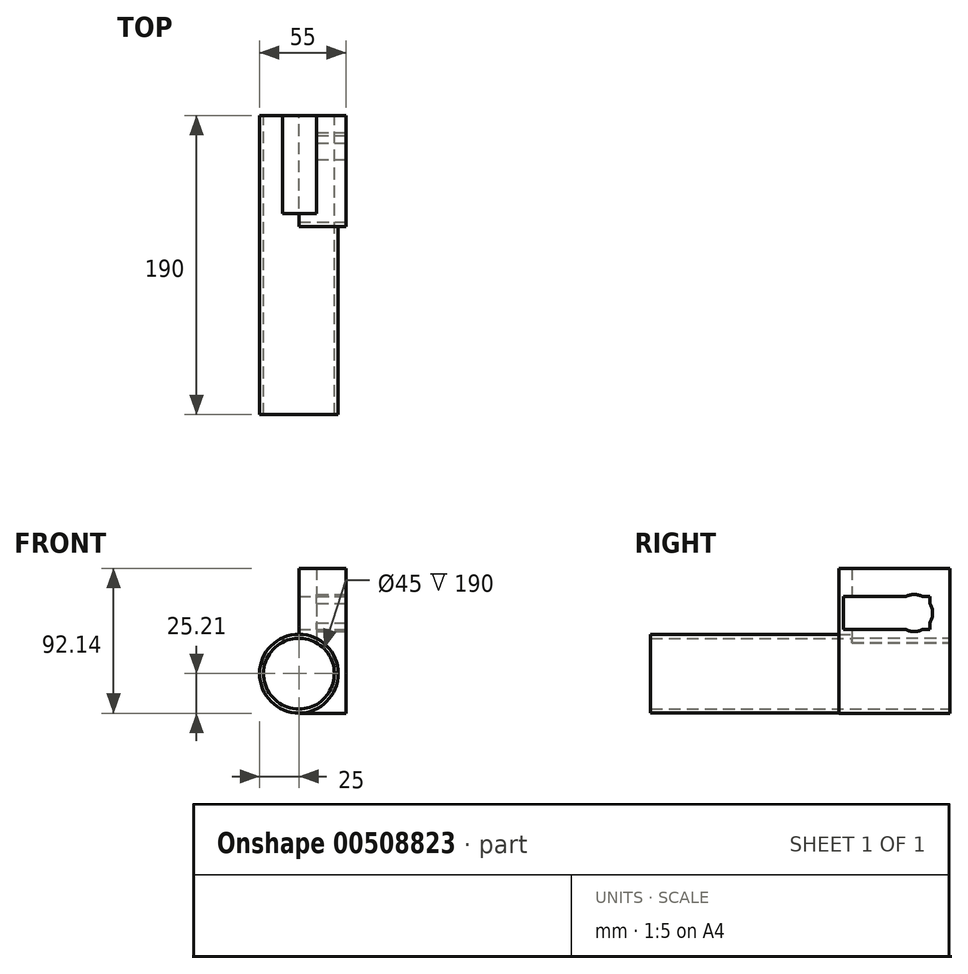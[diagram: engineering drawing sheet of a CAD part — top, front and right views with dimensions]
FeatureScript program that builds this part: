
annotation { "Feature Type Name" : "Feature", "Feature Type Description" : "" }
export const myFeature = defineFeature(function(context is Context, id is Id, definition is map)
    precondition{}
    {
        {
            var Q0;
            Q0=qCreatedBy(makeId("Front.planeOp"),FACE);
            var sketch = newSketch(context, id + "F0", { "sketchPlane" : qUnion([Q0])});
            skCircle(sketch, "E0", {"center": v(0, 0) * mm, "radius": 22.5 * mm});
            skCircle(sketch, "E1", {"center": v(0, 0) * mm, "radius": 25 * mm});
            skSolve(sketch);
        }
        {
            var Q0;
            Q0 = qSketchRegion(id + "F0", true);
            extrude(context, id + "F1", {"entities" : qUnion([Q0]), "depth" : 190 * mm});
        }
        {
            var Q0;
            Q0=qCreatedBy(makeId("Right.planeOp"),FACE);
            var sketch = newSketch(context, id + "F2", { "sketchPlane" : qUnion([Q0])});
            skLineSegment(sketch, "E2.bottom", {"start": v(-70.47, 66.93) * mm, "end": v(0, 66.93) * mm});
            skLineSegment(sketch, "E2.top", {"start": v(-70.47, -25.2) * mm, "end": v(0, -25.2) * mm});
            skLineSegment(sketch, "E2.left", {"start": v(-70.47, 66.93) * mm, "end": v(-70.47, -25.2) * mm});
            skLineSegment(sketch, "E2.right", {"start": v(0, 66.93) * mm, "end": v(0, -25.2) * mm});
            skSolve(sketch);
        }
        {
            var Q0;
            Q0 = qSketchRegion(id + "F2", true);
            extrude(context, id + "F3", {"entities" : qUnion([Q0]), "operationType" : NewBodyOperationType.ADD, "depth" : 30 * mm, "offsetDistance" : 25 * mm});
        }
        {
            var Q0;
            Q0=makeQuery(id+"F3.boolean.opBoolean","SPLIT",FACE,{"disambiguationData":[TD([makeQuery(id+"F1.opExtrude","SWEPT_FACE",FACE,{"disambiguationData":[OSD([sQuery(id+"F0.wireOp",EDGE,"E0")])]})])],"derivedFrom":makeQuery(id+"F3.opExtrude","SWEPT_FACE",FACE,{"disambiguationData":[OSD([sQuery(id+"F2.wireOp",EDGE,"E2.left")])]})});
            var sketch = newSketch(context, id + "F4", { "sketchPlane" : qUnion([Q0])});
            skCircle(sketch, "E3", {"center": v(0, 0) * mm, "radius": 22.5 * mm});
            skSolve(sketch);
        }
        {
            var Q0;
            Q0 = qSketchRegion(id + "F4", true);
            extrude(context, id + "F5", {"entities" : qUnion([Q0]), "operationType" : NewBodyOperationType.REMOVE, "endBound" : BoundingType.SYMMETRIC, "depth" : 200 * mm});
        }
        {
            var Q0;
            Q0=qCreatedBy(makeId("Top.planeOp"),FACE);
            var sketch = newSketch(context, id + "F6", { "sketchPlane" : qUnion([Q0])});
            skLineSegment(sketch, "E4.bottom", {"start": v(11.28, -62.15) * mm, "end": v(-10.5, -62.15) * mm});
            skLineSegment(sketch, "E4.top", {"start": v(11.28, 0) * mm, "end": v(-10.5, 0) * mm});
            skLineSegment(sketch, "E4.left", {"start": v(11.28, -62.15) * mm, "end": v(11.28, 0) * mm});
            skLineSegment(sketch, "E4.right", {"start": v(-10.5, -62.15) * mm, "end": v(-10.5, 0) * mm});
            skSolve(sketch);
        }
        {
            var Q0;
            Q0 = qSketchRegion(id + "F6", true);
            extrude(context, id + "F7", {"entities" : qUnion([Q0]), "operationType" : NewBodyOperationType.REMOVE, "depth" : 100 * mm});
        }
        {
            var Q0;
            Q0=makeQuery(id+"F3.opExtrude","CAP_FACE",FACE,{"disambiguationData":[OSD([sQuery(id+"F2.wireOp",EDGE,"E2.bottom"),sQuery(id+"F2.wireOp",EDGE,"E2.top"),sQuery(id+"F2.wireOp",EDGE,"E2.left"),sQuery(id+"F2.wireOp",EDGE,"E2.right")])],"isStart":false});
            var sketch = newSketch(context, id + "F8", { "sketchPlane" : qUnion([Q0])});
            skLineSegment(sketch, "E5.bottom", {"start": v(-67.63, 49) * mm, "end": v(-12.63, 49) * mm});
            skLineSegment(sketch, "E5.top", {"start": v(-67.63, 28) * mm, "end": v(-12.63, 28) * mm});
            skLineSegment(sketch, "E5.left", {"start": v(-67.63, 49) * mm, "end": v(-67.63, 28) * mm});
            skLineSegment(sketch, "E5.right", {"start": v(-12.63, 49) * mm, "end": v(-12.63, 28) * mm});
            skCircle(sketch, "E6", {"center": v(-22.63, 38.5) * mm, "radius": 11.75 * mm});
            skLineSegment(sketch, "E7.0", {"start": v(0, 19.9) * mm, "end": v(0, -22.5) * mm});
            skLineSegment(sketch, "E8", {"start": v(0, -22.5) * mm, "end": v(-70.47, -22.5) * mm});
            skLineSegment(sketch, "E9", {"start": v(-22.63, 38.5) * mm, "end": v(0, 38.5) * mm});
            skLineSegment(sketch, "E10", {"start": v(-10.88, 38.5) * mm, "end": v(-67.63, 38.5) * mm});
            skSolve(sketch);
        }
        {
            var Q0;
            Q0 = qSketchRegion(id + "F8", true);
            extrude(context, id + "F9", {"entities" : qUnion([Q0]), "operationType" : NewBodyOperationType.REMOVE, "oppositeDirection" : true, "depth" : 100 * mm, "offsetDistance" : 25 * mm});
        }
    });
